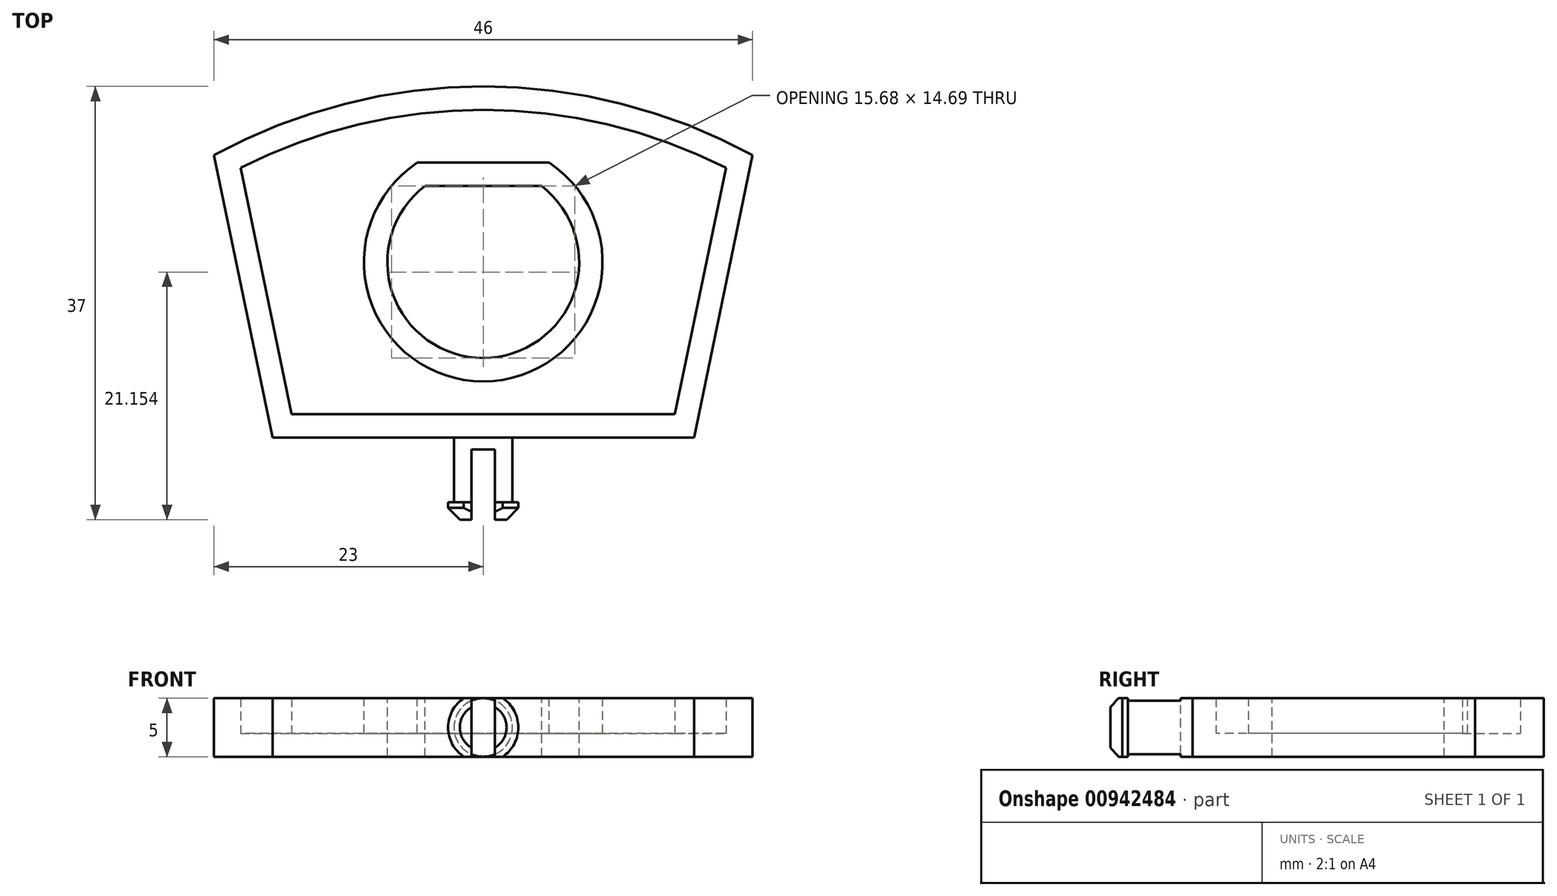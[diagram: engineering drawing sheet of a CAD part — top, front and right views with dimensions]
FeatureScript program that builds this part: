
annotation { "Feature Type Name" : "Feature", "Feature Type Description" : "" }
export const myFeature = defineFeature(function(context is Context, id is Id, definition is map)
    precondition{}
    {
        {
            var Q0;
            Q0=qCreatedBy(makeId("Top.planeOp"),FACE);
            var sketch = newSketch(context, id + "F0", { "sketchPlane" : qUnion([Q0])});
            skLineSegment(sketch, "E0", {"start": v(-23, 24.13) * mm, "end": v(-18, 0) * mm});
            skLineSegment(sketch, "E1", {"start": v(-18, 0) * mm, "end": v(18, 0) * mm});
            skLineSegment(sketch, "E2", {"start": v(18, 0) * mm, "end": v(23, 24.13) * mm});
            skArc(sketch, "E3", {"start": v(23, 24.13) * mm, "mid": v(0, 30) * mm, "end": v(-23, 24.13) * mm});
            skSolve(sketch);
        }
        {
            var Q0;
            Q0 = qSketchRegion(id + "F0", true);
            extrude(context, id + "F1", {"entities" : qUnion([Q0]), "endBound" : BoundingType.SYMMETRIC, "depth" : 5 * mm, "offsetDistance" : 25 * mm});
        }
        {
            var Q0;
            Q0=makeQuery(id+"F1.opExtrude","CAP_FACE",FACE,{"disambiguationData":[OSD([sQuery(id+"F0.wireOp",EDGE,"E0"),sQuery(id+"F0.wireOp",EDGE,"E1"),sQuery(id+"F0.wireOp",EDGE,"E2"),sQuery(id+"F0.wireOp",EDGE,"E3")])],"isStart":false});
            var sketch = newSketch(context, id + "F2", { "sketchPlane" : qUnion([Q0])});
            skLineSegment(sketch, "E4", {"start": v(-4.99, 21.5) * mm, "end": v(4.99, 21.5) * mm});
            skArc(sketch, "E5", {"start": v(-4.99, 21.5) * mm, "mid": v(0, 6.8) * mm, "end": v(4.99, 21.5) * mm});
            skSolve(sketch);
        }
        {
            var Q0;
            Q0 = qSketchRegion(id + "F2", true);
            extrude(context, id + "F3", {"entities" : qUnion([Q0]), "operationType" : NewBodyOperationType.REMOVE, "endBound" : BoundingType.UP_TO_NEXT, "oppositeDirection" : true, "depth" : 25 * mm, "offsetDistance" : 25 * mm});
        }
        {
            var Q0;
            Q0=makeQuery(id+"F1.opExtrude","CAP_FACE",FACE,{"disambiguationData":[OSD([sQuery(id+"F0.wireOp",EDGE,"E0"),sQuery(id+"F0.wireOp",EDGE,"E1"),sQuery(id+"F0.wireOp",EDGE,"E2"),sQuery(id+"F0.wireOp",EDGE,"E3")])],"isStart":false});
            shell(context, id + "F4", {"entities" : qUnion([Q0]), "thickness" : 2 * mm});
        }
        {
            var Q0;
            Q0=qCreatedBy(makeId("Right.planeOp"),FACE);
            var sketch = newSketch(context, id + "F5", { "sketchPlane" : qUnion([Q0])});
            skLineSegment(sketch, "E6", {"start": v(0, 0) * mm, "end": v(-7, 0) * mm});
            skLineSegment(sketch, "E7", {"start": v(-7, 0) * mm, "end": v(-7, 3) * mm});
            skLineSegment(sketch, "E8", {"start": v(-7, 3) * mm, "end": v(-5.5, 3) * mm});
            skLineSegment(sketch, "E9", {"start": v(-5.5, 3) * mm, "end": v(-5.5, 2.5) * mm});
            skLineSegment(sketch, "E10", {"start": v(-5.5, 2.5) * mm, "end": v(0, 2.5) * mm});
            skLineSegment(sketch, "E11", {"start": v(0, 2.5) * mm, "end": v(0, 0) * mm});
            skSolve(sketch);
        }
        {
            var Q0;
            Q0=makeQuery(id+"F5.imprint","IMPRINT",FACE,{"disambiguationData":[TD([[makeQuery(id+"F5.imprint","IMPRINT",EDGE,{"derivedFrom":sQuery(id+"F5.wireOp",EDGE,"E6")}),-1.0]])]});
            var Q1;
            Q1=sQuery(id+"F5.wireOp",EDGE,"E6");
            revolve(context, id + "F6", {"operationType" : NewBodyOperationType.ADD, "surfaceOperationType" : NewSurfaceOperationType.NEW, "entities" : qUnion([Q0]), "axis" : qUnion([Q1]), "revolveType" : RevolveType.FULL});
        }
        {
            var Q0;
            Q0=makeQuery(id+"F6.opRevolve","SWEPT_EDGE",EDGE,{"disambiguationData":[OSD([sQuery(id+"F5.wireOp",EDGE,"E7"),sQuery(id+"F5.wireOp",EDGE,"E8")])]});
            chamfer(context, id + "F7", {"entities" : qUnion([Q0]), "width" : 1 * mm, "tangentPropagation" : true});
        }
        {
            var Q0;
            Q0=makeQuery(id+"F6.opRevolve","SWEPT_FACE",FACE,{"disambiguationData":[OSD([sQuery(id+"F5.wireOp",EDGE,"E7")])]});
            var sketch = newSketch(context, id + "F8", { "sketchPlane" : qUnion([Q0])});
            skLineSegment(sketch, "E12.bottom", {"start": v(-23.51, -2.5) * mm, "end": v(24.64, -2.5) * mm});
            skLineSegment(sketch, "E12.top", {"start": v(-23.51, 2.5) * mm, "end": v(24.64, 2.5) * mm});
            skLineSegment(sketch, "E12.left", {"start": v(-23.51, -2.5) * mm, "end": v(-23.51, 2.5) * mm});
            skLineSegment(sketch, "E12.right", {"start": v(24.64, -2.5) * mm, "end": v(24.64, 2.5) * mm});
            skSolve(sketch);
        }
        {
            var Q0;
            Q0 = qSketchRegion(id + "F8", true);
            extrude(context, id + "F9", {"entities" : qUnion([Q0]), "operationType" : NewBodyOperationType.INTERSECT, "endBound" : BoundingType.THROUGH_ALL, "oppositeDirection" : true, "depth" : 25 * mm, "offsetDistance" : 25 * mm});
        }
        {
            var Q0;
            Q0=makeQuery(id+"F6.opRevolve","SWEPT_FACE",FACE,{"disambiguationData":[OSD([sQuery(id+"F5.wireOp",EDGE,"E7")])]});
            var sketch = newSketch(context, id + "F10", { "sketchPlane" : qUnion([Q0])});
            skLineSegment(sketch, "E13.bottom", {"start": v(-1, -4.99) * mm, "end": v(1, -4.99) * mm});
            skLineSegment(sketch, "E13.top", {"start": v(-1, 4.16) * mm, "end": v(1, 4.16) * mm});
            skLineSegment(sketch, "E13.left", {"start": v(-1, -4.99) * mm, "end": v(-1, 4.16) * mm});
            skLineSegment(sketch, "E13.right", {"start": v(1, -4.99) * mm, "end": v(1, 4.16) * mm});
            skSolve(sketch);
        }
        {
            var Q0;
            Q0 = qSketchRegion(id + "F10", true);
            extrude(context, id + "F11", {"entities" : qUnion([Q0]), "operationType" : NewBodyOperationType.REMOVE, "oppositeDirection" : true, "depth" : 6 * mm, "offsetDistance" : 25 * mm});
        }
    });
